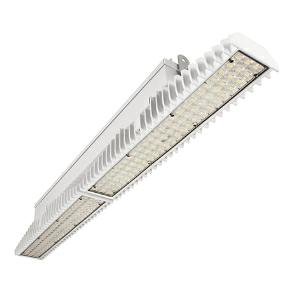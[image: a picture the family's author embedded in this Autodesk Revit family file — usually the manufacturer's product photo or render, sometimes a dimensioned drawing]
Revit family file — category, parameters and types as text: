
# Revit family: 3f_filippi_-_3f_lem_ampio_3f_filippi_-_58885_a0811_-_3f_lem_1_1_led_100_cr_ampio___vt_36d7
name_source: partatom
category: Lighting Fixtures
units: mm (PartAtom-declared; Revit-internal decimal feet)

## family parameters
Cut with Voids When Loaded = No
Host = Face
Light Source = No
Part Type = Normal
Room Calculation Point = No
Round Connector Dimension = Use Diameter
Shared = No

## types (1)
- 3F Filippi - 3F LEM Ampio (1 x LED, 15821 lm, 109 W, 4000 K)
    Apparent Load = 109 VA
    Approval mark = CE
    CIE Flux Codes = 60 92 99 100 100
    Color Rendering = 80
    Color Temperature = 4000 K
    Control Gear = Electronic ballast
    Default Elevation = 1800 mm
    Description = Industrial luminaire with high light output and high luminous efficiency designed with the most innovative technologies for environments with temperature up to 55°C.

ILLUMINOTECHNICAL
Luminous efficiency 100% (DLOR 99%, ULOR 1%).
Initial luminous flux of the luminaire 15821 lm.
Direct symmetric wide distribution: the illuminated area has a rectangular shape.
Installation Interdistance Transv.D = 1.58 x hu - Long.D = 1.45 x hu.
Tabular UGR (CIE 117 - 4H-8H; S=0.25H; 70/50/20): RUG 25.9 - 26.8.
Beam angle: 93° - 99°.
Luminous efficacy 145 lm/W.
Lifetime (L93/B10): 30000 h. (tq+25°C)
Lifetime (L90/B10): 50000 h. (tq+25°C)
Lifetime (L85/B10): 80000 h. (tq+25°C)
Lifetime (L80/B10): 100000 h. (tq+25°C)
Lifetime (L85/B10): 50000 h. (tq+55°C)
Sudden decreased luminous flux after 50000 hours: 0% (C0).
Photobiological safety in compliance with IEC/TR 62778: RG0 risk exempt, (IEC 62471).
In compliance with IEC/EN 62722-2-1 - IEC/EN 62717 standards.

SOURCE
2 Mid-Power linear LED modules 50W/840.
Energy efficiency class (UE 2019/2020 - UE 2019/2015): C.
CIE 13.3 Colour rendering index: CRI >80 (R9 <50%).
IES TM-30 Fidelity Index: Rf = 84 Rg = 95.
CCT nominal colour temperature 4000 K.
Colour initial tolerance (MacAdam): SDCM 3.

MECHANICAL
Passive modular heatsinks in die-casted aluminium, painted in white colour.
To optimize the thermal management of the LED module, the heatsinks are oversized and provided with self-cleaning of cooling fins.
Wiring body in aluminium and galvanised steel anchored solidly to the sinks and thermally separated.
3F Lens lenses with high luminous efficiency, transparent methacrylate (PMMA), fixed to the LED modules.
Fixing brackets in stainless steel.
Luminaire with limited surface temperature. - D - (EN 60598-2-24)
Dimensions: 1099x115 mm, height 154 mm. Weight 11.454 kg.
IP65 protection degree.
Mechanical strength to impacts IK06 (1 joule).
Glow-wire test resistance 650°C.

ELECTRICAL
Halogen Free electronic wiring 230V-50/60Hz, power factor 0.97, THD <25%, constant output current, class I, 1 driver.
Power of the luminaire 109 W.
ENEC - CE.
SAFE FLICKER: PstLM=<1 and SVM=<0.4 (IEC TR 61547-1 and IEC TR 63158), to ensure a more comfortable and safe light.
Luminaire compliant with EN 60598-2-22 for power supply from a centralised emergency system CPSS (Central Power Supply System), not incorporated in the luminaire - high risk areas excluded. The default power and flux are 100% in AC and 100% in DC.
Ambient temperature from -30°C to +55°C.
Temperature class T6 max 85°C.
Quick connection via M20 3P connector with 9-13 mm tightening range.
Power unit positioned on a separate compartment by the LED module to ensure optimum temperatures of cabling components, to be inspectable and maintainable.
Relative humidity UR: <85%.

INSTALLATION
Ceiling / Suspended / Wall.
All accessories dedicated to this product are available on the Catalog and on our website www.3F-Filippi.com.

ACCESSORIES
A0811 - VT transparent glass, tempered, not flammable, with sealing gasket.
One required for each light module. The pack contains 10 pieces.

APPLICATIONS
In commercial environments, exhibition and industrial areas, stores, open areas.
Applications with high ambient temperature up to 55°C.
Environments in which it is necessary a total protection against falling fragments (eg environments with foodstuffs or machines with moving parts or with extreme temperature changes), use luminaires with polycarbonate lenses.

WARNING
Fixture not suitable for cold stores with an ambient temperature <0°C and/or relative humidity >85%.
Luminaire designed for disposal/recycling at end-of-life.
Replaceable (LED only) light source by a professional. Replaceable control gear by a professional.
    Height = 154 mm
    Lamp = 1 x LED
    Lamp Light Flux = 15821 lm
    Lamp Power = 109 W
    Lamp count = 1
    Length = 1099 mm
    Lifetime = 50000 h
    Luminous efficacy = 145 lm/W
    Manufacturer = 3F Filippi
    ModVariant = No
    Model = 3F Filippi - 58885+A0811 - 3F LEM 1+1 LED 100 CR AMPIO + VT
    Mounting Place = Ceiling
    Mounting Type = Pendant
    Number of Poles = 1
    OnlyDefault = Yes
    Power Factor = 1
    Product Name = 3F Filippi - 3F LEM Ampio
    Product group = pendant luminaire
    ProductGroupID = 9
    Protection Class = Protection class I
    Protection Degree = IP 65
    RLX_Detail_Level = 1
    RLX_Emergency_Light_Flux = 0 lm
    RLX_Emergency_Type = 0
    RLX_Emergency_Type_DB = No
    RlxData = <blob elided: 97961 chars, md5=c9c52b90>
    Socket = socket
    Standby Power = 0 W
    System Light Flux = 15821 lm
    System Power = 109 W
    Type Comments = Product without accessories
    Type Image = 3f_filippi_-_lem_11__a0811.jpg
    URL = http://relux.com
    VarID = ---
    Voltage = 0 V
    Weight = 0.00 kg
    Width = 115 mm

## geometry (parser evidence)
native form markers: Blend x4, Sweep x12
no freeform markers — native parametric forms only
